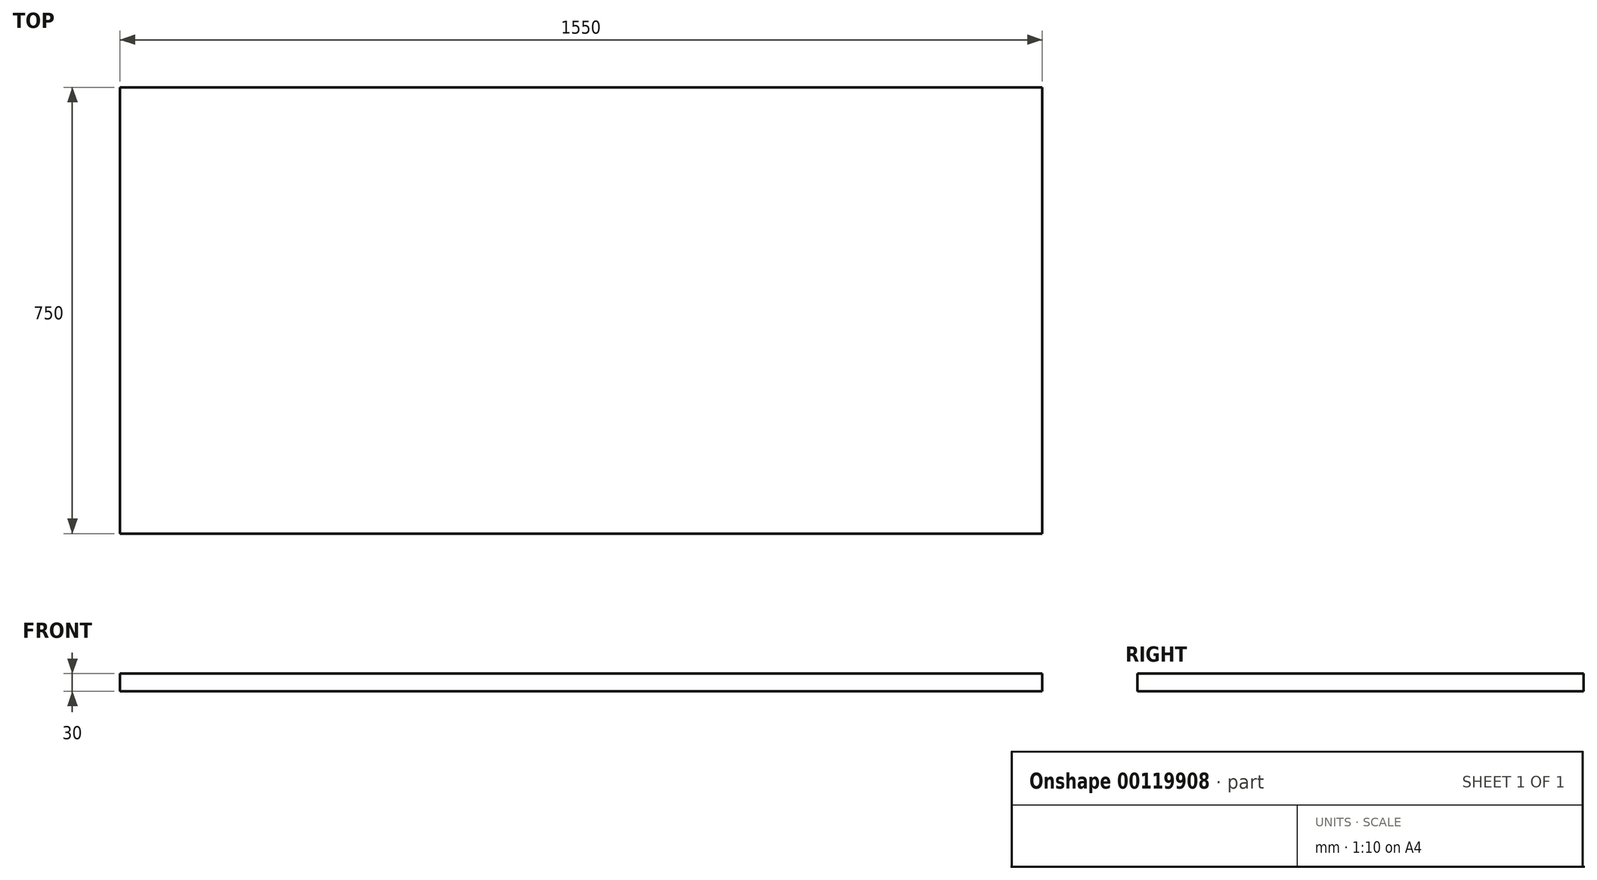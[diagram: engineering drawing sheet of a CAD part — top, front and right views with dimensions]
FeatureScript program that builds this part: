
annotation { "Feature Type Name" : "Feature", "Feature Type Description" : "" }
export const myFeature = defineFeature(function(context is Context, id is Id, definition is map)
    precondition{}
    {
        {
            var Q0;
            Q0=qCreatedBy(makeId("Top.planeOp"),FACE);
            var sketch = newSketch(context, id + "F0", { "sketchPlane" : qUnion([Q0])});
            skLineSegment(sketch, "E0.bottom", {"start": v(775, -375) * mm, "end": v(-775, -375) * mm});
            skLineSegment(sketch, "E0.top", {"start": v(775, 375) * mm, "end": v(-775, 375) * mm});
            skLineSegment(sketch, "E0.left", {"start": v(775, -375) * mm, "end": v(775, 375) * mm});
            skLineSegment(sketch, "E0.right", {"start": v(-775, -375) * mm, "end": v(-775, 375) * mm});
            skPoint(sketch, "E0.middle", {"position": v(0, 0) * mm});
            skSolve(sketch);
        }
        {
            var Q0;
            Q0 = qSketchRegion(id + "F0", true);
            extrude(context, id + "F1", {"entities" : qUnion([Q0]), "depth" : 30 * mm});
        }
        {
            var Q0;
            Q0=makeQuery(id+"F1.opExtrude","CAP_FACE",FACE,{"disambiguationData":[OSD([sQuery(id+"F0.wireOp",EDGE,"E0.bottom"),sQuery(id+"F0.wireOp",EDGE,"E0.top"),sQuery(id+"F0.wireOp",EDGE,"E0.left"),sQuery(id+"F0.wireOp",EDGE,"E0.right")])],"isStart":true});
            var sketch = newSketch(context, id + "F2", { "sketchPlane" : qUnion([Q0])});
            skLineSegment(sketch, "E1", {"start": v(-775, 286.1) * mm, "end": v(775, 286.1) * mm, "construction": true});
            skLineSegment(sketch, "E2", {"start": v(-686.1, 375) * mm, "end": v(-686.1, -375) * mm, "construction": true});
            skLineSegment(sketch, "E3", {"start": v(0, 375) * mm, "end": v(0, -375) * mm, "construction": true});
            skPoint(sketch, "E4", {"position": v(-686.1, 286.1) * mm});
            skPoint(sketch, "E5.MirrorP", {"position": v(686.1, 286.1) * mm});
            skPoint(sketch, "E6", {"position": v(0, 286.1) * mm});
            skLineSegment(sketch, "E7", {"start": v(-775, 0) * mm, "end": v(775, 0) * mm, "construction": true});
            skPoint(sketch, "E8.MirrorP", {"position": v(686.1, -286.1) * mm});
            skPoint(sketch, "E9.MirrorP", {"position": v(0, -286.1) * mm});
            skPoint(sketch, "E10.MirrorP", {"position": v(-686.1, -286.1) * mm});
            skSolve(sketch);
        }
    });
